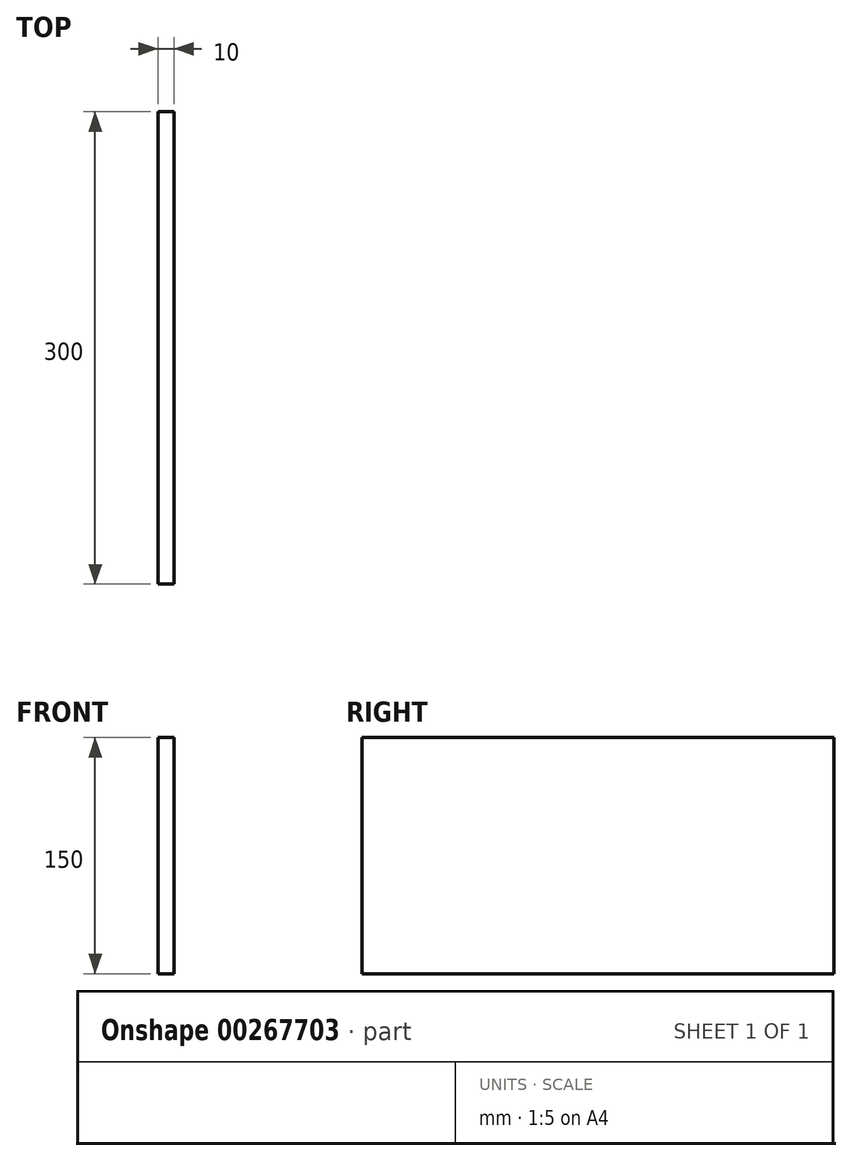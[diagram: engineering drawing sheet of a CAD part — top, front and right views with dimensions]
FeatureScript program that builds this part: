
annotation { "Feature Type Name" : "Feature", "Feature Type Description" : "" }
export const myFeature = defineFeature(function(context is Context, id is Id, definition is map)
    precondition{}
    {
        {
            var Q0;
            Q0=qCreatedBy(makeId("Front.planeOp"),FACE);
            var sketch = newSketch(context, id + "F0", { "sketchPlane" : qUnion([Q0])});
            skLineSegment(sketch, "E0.bottom", {"start": v(5, 75) * mm, "end": v(-5, 75) * mm});
            skLineSegment(sketch, "E0.top", {"start": v(5, -75) * mm, "end": v(-5, -75) * mm});
            skLineSegment(sketch, "E0.left", {"start": v(5, 75) * mm, "end": v(5, -75) * mm});
            skLineSegment(sketch, "E0.right", {"start": v(-5, 75) * mm, "end": v(-5, -75) * mm});
            skPoint(sketch, "E0.middle", {"position": v(0, 0) * mm});
            skSolve(sketch);
        }
        {
            var Q0;
            Q0 = qSketchRegion(id + "F0", true);
            extrude(context, id + "F1", {"entities" : qUnion([Q0]), "oppositeDirection" : true, "depth" : 300 * mm});
        }
    });
